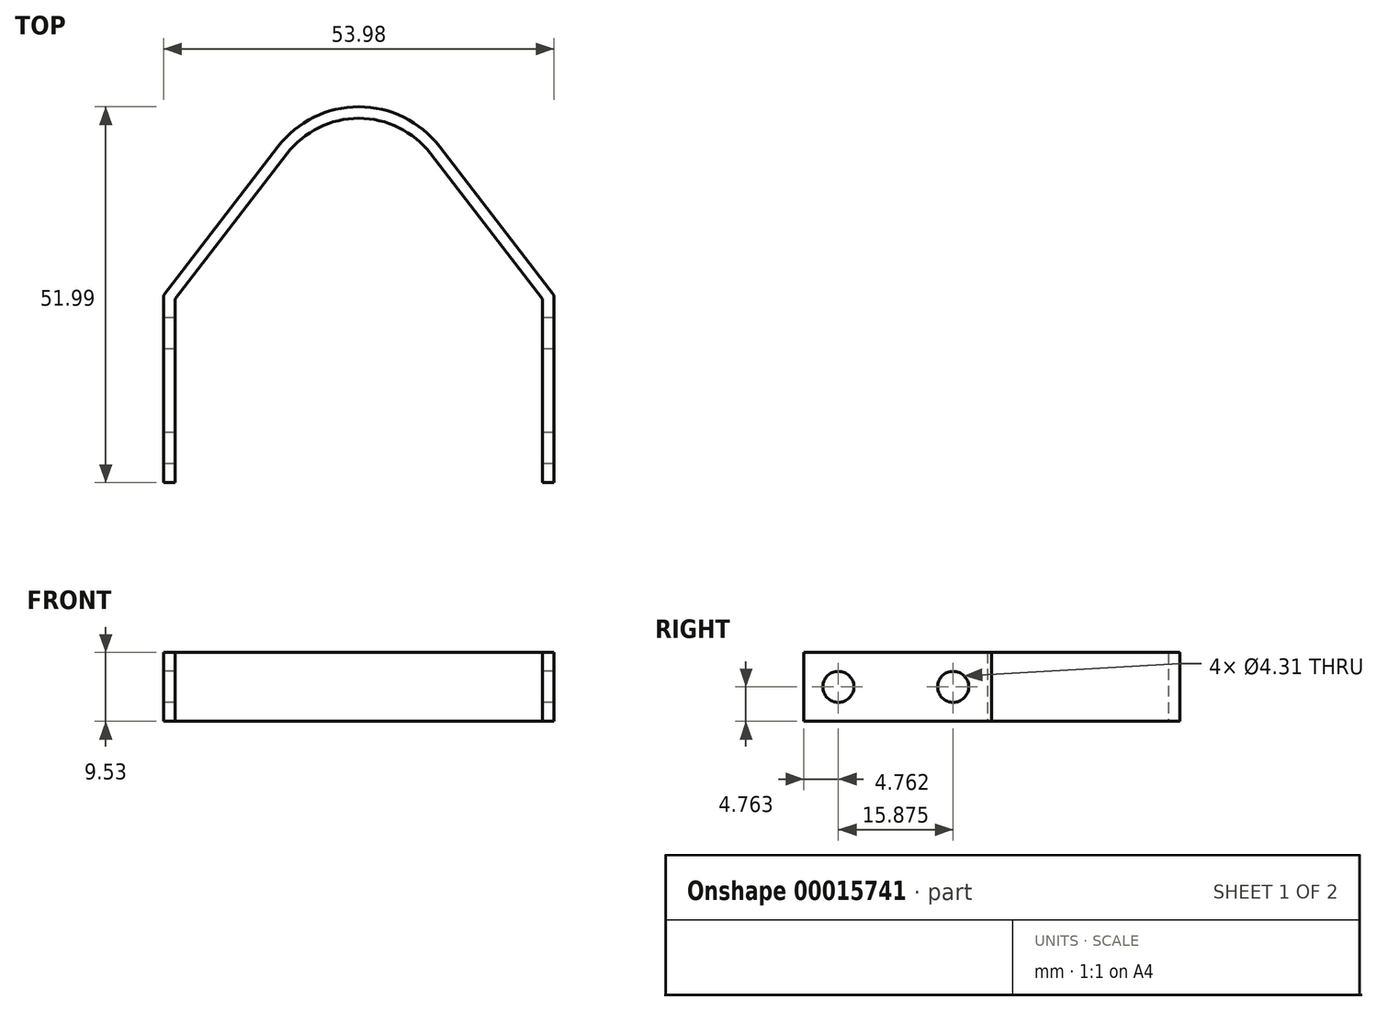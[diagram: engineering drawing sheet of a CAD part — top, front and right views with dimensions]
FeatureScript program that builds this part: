
annotation { "Feature Type Name" : "Feature", "Feature Type Description" : "" }
export const myFeature = defineFeature(function(context is Context, id is Id, definition is map)
    precondition{}
    {
        {
            var Q0;
            Q0=qCreatedBy(makeId("Top.planeOp"),FACE);
            var sketch = newSketch(context, id + "F0", { "sketchPlane" : qUnion([Q0])});
            skArc(sketch, "E0", {"start": v(9.9, 7.63) * mm, "mid": v(0, 12.5) * mm, "end": v(-9.9, 7.63) * mm});
            skArc(sketch, "E1", {"start": v(-9.9, 7.63) * mm, "mid": v(0, -12.5) * mm, "end": v(9.9, 7.63) * mm, "construction": true});
            skLineSegment(sketch, "E2", {"start": v(0, 0) * mm, "end": v(0, -12.5) * mm, "construction": true});
            skLineSegment(sketch, "E3", {"start": v(25.4, -12.5) * mm, "end": v(-25.4, -12.5) * mm, "construction": true});
            skLineSegment(sketch, "E4", {"start": v(9.9, 7.63) * mm, "end": v(25.4, -12.5) * mm});
            skLineSegment(sketch, "E5.top", {"start": v(25.4, -37.9) * mm, "end": v(26.99, -37.9) * mm});
            skLineSegment(sketch, "E5.left", {"start": v(25.4, -12.5) * mm, "end": v(25.4, -37.9) * mm});
            skLineSegment(sketch, "E5.right", {"start": v(26.99, -11.96) * mm, "end": v(26.99, -37.9) * mm});
            skLineSegment(sketch, "E6.top", {"start": v(-25.4, -37.9) * mm, "end": v(-26.99, -37.9) * mm});
            skLineSegment(sketch, "E6.left", {"start": v(-25.4, -12.5) * mm, "end": v(-25.4, -37.9) * mm});
            skLineSegment(sketch, "E6.right", {"start": v(-26.99, -11.96) * mm, "end": v(-26.99, -37.9) * mm});
            skArc(sketch, "E7", {"start": v(11.16, 8.6) * mm, "mid": v(0, 14.09) * mm, "end": v(-11.16, 8.6) * mm});
            skLineSegment(sketch, "E8", {"start": v(11.16, 8.6) * mm, "end": v(26.99, -11.96) * mm});
            skLineSegment(sketch, "E9", {"start": v(-9.9, 7.63) * mm, "end": v(-25.4, -12.5) * mm});
            skLineSegment(sketch, "E10", {"start": v(-11.16, 8.6) * mm, "end": v(-26.99, -11.96) * mm});
            skSolve(sketch);
        }
        {
            var Q0;
            Q0 = qSketchRegion(id + "F0", true);
            extrude(context, id + "F1", {"entities" : qUnion([Q0]), "depth" : 9.52 * mm});
        }
        {
            var Q0;
            Q0=makeQuery(id+"F1.opExtrude","SWEPT_FACE",FACE,{"disambiguationData":[OSD([sQuery(id+"F0.wireOp",EDGE,"E5.left")])]});
            var sketch = newSketch(context, id + "F2", { "sketchPlane" : qUnion([Q0])});
            skLineSegment(sketch, "E11", {"start": v(12.5, 4.76) * mm, "end": v(17.26, 4.76) * mm, "construction": true});
            skLineSegment(sketch, "E12", {"start": v(17.26, 4.76) * mm, "end": v(33.14, 4.76) * mm, "construction": true});
            skLineSegment(sketch, "E13", {"start": v(33.14, 4.76) * mm, "end": v(37.9, 4.76) * mm, "construction": true});
            skCircle(sketch, "E14", {"center": v(17.26, 4.76) * mm, "radius": 2.15 * mm});
            skCircle(sketch, "E15", {"center": v(33.14, 4.76) * mm, "radius": 2.15 * mm});
            skSolve(sketch);
        }
        {
            var Q0;
            Q0 = qSketchRegion(id + "F2", true);
            var Q1;
            Q1=makeQuery(id+"F1.opExtrude","SWEPT_FACE",FACE,{"disambiguationData":[OSD([sQuery(id+"F0.wireOp",EDGE,"E5.right")])]});
            var Q2;
            Q2=makeQuery(id+"F1.opExtrude","SWEPT_FACE",FACE,{"disambiguationData":[OSD([sQuery(id+"F0.wireOp",EDGE,"E6.right")])]});
            extrude(context, id + "F3", {"entities" : qUnion([Q0]), "operationType" : NewBodyOperationType.REMOVE, "endBound" : BoundingType.UP_TO_SURFACE, "oppositeDirection" : true, "endBoundEntityFace" : qUnion([Q1]), "depth" : 25.4 * mm, "hasSecondDirection" : true, "secondDirectionBound" : BoundingType.UP_TO_SURFACE, "secondDirectionOppositeDirection" : false, "secondDirectionBoundEntityFace" : qUnion([Q2]), "secondDirectionDepth" : 25.4 * mm});
        }
    });
